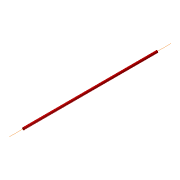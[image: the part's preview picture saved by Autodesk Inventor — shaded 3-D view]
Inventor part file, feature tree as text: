
AUTODESK INVENTOR PART (.ipt)
format: ipt  version: unknown  size: 156,160 bytes
history: native  units: in
note: dims shown in document units (in); Inventor stores cm internally (conversion verified against a paired STEP export)
features: extrude x1, sketch x1
ambient origin geometry x8: Origin, YZ Plane, XZ Plane, XY Plane, X Axis, Y Axis, Z Axis, Center Point
feature tree (2):
  extrude  "Extrusion8"  Depth=2.3622in TaperAngle=0.0deg
  sketch  "Sketch23"  dims[d72=0.0394in d73=2.3622in d74=0.0in]
